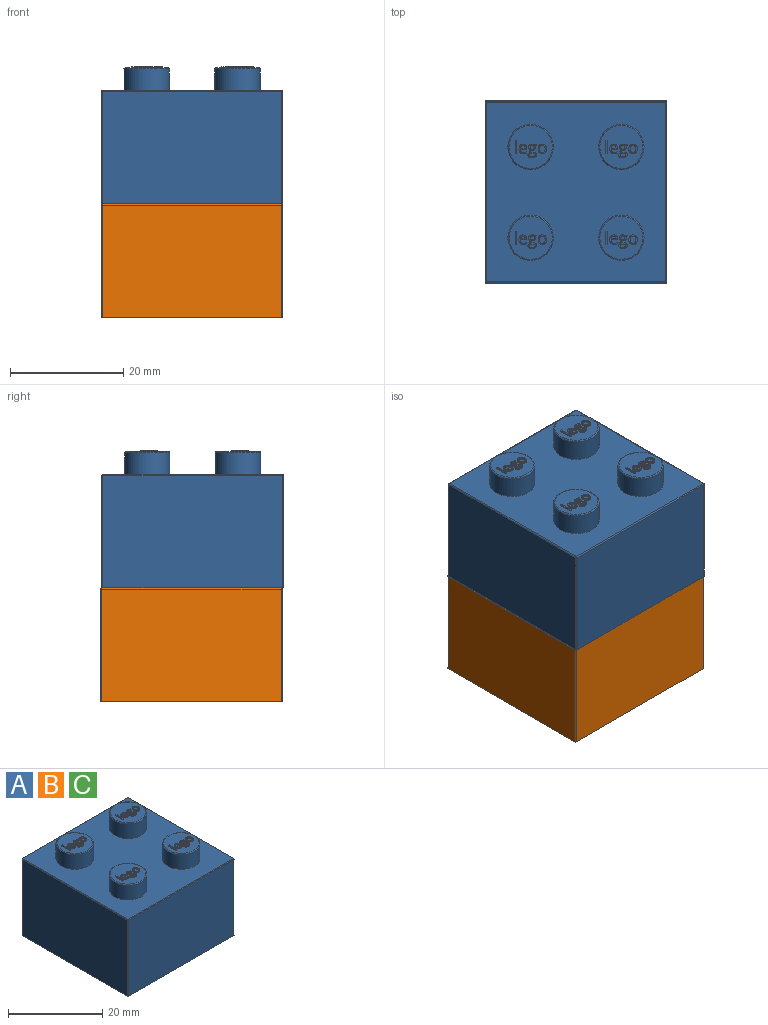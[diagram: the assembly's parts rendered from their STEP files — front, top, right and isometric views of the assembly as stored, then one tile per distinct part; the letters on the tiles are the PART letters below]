
ASSEMBLY  parts=3 mates=1
PART A: 411 faces, bbox 32x32x24.2 mm
  f0: plane 0.73x0.72mm, normal (0,0,1), area 0.4mm2, adj f12,f13,f14,f15,f16,f17
  f1: plane 1.04x0.58mm, normal (0,0,1), area 0.5mm2, adj f18,f19,f20,f21,f22,f23,f24,f25
  f2: plane 1.27x0.98mm, normal (0,0,1), area 1mm2, adj f57,f58,f59,f60,f61,f62,f63,f64
  f3: plane 0.85x0.48mm, normal (0,0,1), area 0.3mm2, adj f89,f90,f91,f92,f93
  f4: plane 0.73x0.72mm, normal (0,0,1), area 0.4mm2, adj f100,f101,f102,f103,f104,f105
  f5: plane 1.04x0.58mm, normal (0,0,1), area 0.5mm2, adj f106,f107,f108,f109,f110,f111,f112,f113
  f6: plane 1.27x0.98mm, normal (0,0,1), area 1mm2, adj f145,f146,f147,f148,f149,f150,f151,f152
  f7: plane 0.85x0.48mm, normal (0,0,1), area 0.3mm2, adj f177,f178,f179,f180,f181
  f8: plane 0.73x0.72mm, normal (0,0,1), area 0.4mm2, adj f188,f189,f190,f191,f192,f193
  f9: plane 1.04x0.58mm, normal (0,0,1), area 0.5mm2, adj f194,f195,f196,f197,f198,f199,f200,f201
  f10: plane 1.27x0.98mm, normal (0,0,1), area 1mm2, adj f233,f234,f235,f236,f237,f238,f239,f240
  f11: plane 0.85x0.48mm, normal (0,0,1), area 0.3mm2, adj f265,f266,f267,f268,f269
  f12: extruded ~0.27x0.2mm, area 0.1mm2, adj f0,f13,f17,f56
  f13: extruded ~0.36x0.35mm, area 0.1mm2, adj f0,f12,f14,f56
  f14: extruded ~0.37x0.36mm, area 0.1mm2, adj f0,f13,f15,f56
  f15: extruded ~0.27x0.2mm, area 0.1mm2, adj f0,f14,f16,f56
  f16: extruded ~0.28x0.2mm, area 0.1mm2, adj f0,f15,f17,f56
  f17: extruded ~0.26x0.2mm, area 0.1mm2, adj f0,f12,f16,f56
  f18: extruded ~0.32x0.2mm, area 0.1mm2, adj f1,f19,f26,f56
  f19: extruded ~0.46x0.2mm, area 0.1mm2, adj f1,f18,f20,f56
  f20: extruded ~0.25x0.2mm, area 0.1mm2, adj f1,f19,f21,f56
  f21: extruded ~0.2x0.18mm, area 0mm2, adj f1,f20,f22,f56
  f22: extruded ~0.31x0.2mm, area 0.1mm2, adj f1,f21,f23,f56
  f23: plane 0.3x0.2mm, normal (0,-1,0), area 0.1mm2, adj f1,f22,f24,f56
  f24: extruded ~0.26x0.2mm, area 0.1mm2, adj f1,f23,f25,f56
  f25: extruded ~0.23x0.2mm, area 0.1mm2, adj f1,f24,f26,f56
  f26: extruded ~0.2x0.2mm, area 0mm2, adj f1,f18,f25,f56
  f27: plane 0.3x0.2mm, normal (0.12,-0.99,0), area 0.1mm2, adj f28,f55,f56,f278
  f28: extruded ~0.2x0.14mm, area 0mm2, adj f27,f29,f56,f278
  f29: extruded ~0.2x0.19mm, area 0mm2, adj f28,f30,f56,f278
  f30: extruded ~0.38x0.2mm, area 0.1mm2, adj f29,f31,f56,f278
  f31: extruded ~0.45x0.2mm, area 0.1mm2, adj f30,f32,f56,f278
  f32: extruded ~0.2x0.14mm, area 0mm2, adj f31,f33,f56,f278
  f33: extruded ~0.21x0.2mm, area 0.1mm2, adj f32,f34,f56,f278
  f34: extruded ~0.2x0.1mm, area 0mm2, adj f33,f35,f56,f278
  f35: extruded ~0.2x0.19mm, area 0mm2, adj f34,f36,f56,f278
  f36: plane 0.29x0.2mm, normal (0,1,0), area 0.1mm2, adj f35,f37,f56,f278
  f37: extruded ~0.41x0.2mm, area 0.1mm2, adj f36,f38,f56,f278
  f38: extruded ~0.32x0.2mm, area 0.1mm2, adj f37,f39,f56,f278
  f39: extruded ~0.41x0.22mm, area 0.1mm2, adj f38,f40,f56,f278
  f40: extruded ~0.63x0.2mm, area 0.1mm2, adj f39,f41,f56,f278
  f41: extruded ~0.49x0.2mm, area 0.1mm2, adj f40,f42,f56,f278
  f42: extruded ~0.34x0.2mm, area 0.1mm2, adj f41,f43,f56,f278
  f43: extruded ~0.26x0.2mm, area 0.1mm2, adj f42,f44,f56,f278
  f44: extruded ~0.27x0.2mm, area 0.1mm2, adj f43,f45,f56,f278
  f45: extruded ~0.2x0.1mm, area 0mm2, adj f44,f46,f56,f278
  f46: extruded ~0.2x0.14mm, area 0mm2, adj f45,f47,f56,f278
  f47: extruded ~0.2x0.16mm, area 0mm2, adj f46,f48,f56,f278
  f48: extruded ~0.2x0.15mm, area 0mm2, adj f47,f49,f56,f278
  f49: extruded ~0.21x0.2mm, area 0.1mm2, adj f48,f50,f56,f278
  f50: extruded ~0.29x0.2mm, area 0.1mm2, adj f49,f51,f56,f278
  f51: extruded ~0.41x0.2mm, area 0.1mm2, adj f50,f52,f56,f278
  f52: extruded ~0.45x0.2mm, area 0.1mm2, adj f51,f53,f56,f278
  f53: extruded ~0.23x0.2mm, area 0mm2, adj f52,f54,f56,f278
  f54: plane 0.56x0.2mm, normal (0,1,0), area 0.1mm2, adj f53,f55,f56,f278
  f55: plane 0.2x0.16mm, normal (1,0,0), area 0mm2, adj f27,f54,f56,f278
  f56: plane 2.39x1.53mm, normal (0,0,1), area 1.5mm2, adj f12,f13,f14,f15,f16,f17,f18,f19
  f57: extruded ~0.37x0.2mm, area 0.1mm2, adj f2,f58,f64,f74
  f58: extruded ~0.37x0.2mm, area 0.1mm2, adj f2,f57,f59,f74
  f59: extruded ~0.48x0.2mm, area 0.1mm2, adj f2,f58,f60,f74
  f60: extruded ~0.47x0.2mm, area 0.1mm2, adj f2,f59,f61,f74
  f61: extruded ~0.37x0.2mm, area 0.1mm2, adj f2,f60,f62,f74
  f62: extruded ~0.37x0.2mm, area 0.1mm2, adj f2,f61,f63,f74
  f63: extruded ~0.47x0.2mm, area 0.1mm2, adj f2,f62,f64,f74
  f64: extruded ~0.48x0.2mm, area 0.1mm2, adj f2,f57,f63,f74
  f65: extruded ~0.55x0.22mm, area 0.1mm2, adj f66,f73,f74,f278
  f66: extruded ~0.39x0.2mm, area 0.1mm2, adj f65,f67,f74,f278
  f67: extruded ~0.29x0.26mm, area 0.1mm2, adj f66,f68,f74,f278
  f68: extruded ~0.45x0.2mm, area 0.1mm2, adj f67,f69,f74,f278
  f69: extruded ~0.62x0.2mm, area 0.1mm2, adj f68,f70,f74,f278
  f70: extruded ~0.55x0.22mm, area 0.1mm2, adj f69,f71,f74,f278
  f71: extruded ~0.54x0.23mm, area 0.1mm2, adj f70,f72,f74,f278
  f72: extruded ~0.61x0.2mm, area 0.1mm2, adj f71,f73,f74,f278
  f73: extruded ~0.62x0.2mm, area 0.1mm2, adj f65,f72,f74,f278
  f74: plane 1.69x1.49mm, normal (0,0,1), area 1mm2, adj f57,f58,f59,f60,f61,f62,f63,f64
  f75: extruded ~0.57x0.22mm, area 0.1mm2, adj f76,f88,f94,f278
  f76: extruded ~0.28x0.2mm, area 0.1mm2, adj f75,f77,f94,f278
  f77: extruded ~0.25x0.2mm, area 0.1mm2, adj f76,f78,f94,f278
  f78: plane 0.22x0.2mm, normal (1,0,0), area 0mm2, adj f77,f79,f94,f278
  f79: extruded ~0.52x0.2mm, area 0.1mm2, adj f78,f80,f94,f278
  f80: extruded ~0.39x0.2mm, area 0.1mm2, adj f79,f81,f94,f278
  f81: extruded ~0.43x0.2mm, area 0.1mm2, adj f80,f82,f94,f278
  f82: plane 1.12x0.2mm, normal (0,-1,0), area 0.2mm2, adj f81,f83,f94,f278
  f83: plane 0.2x0.16mm, normal (1,0,0), area 0mm2, adj f82,f84,f94,f278
  f84: extruded ~0.53x0.2mm, area 0.1mm2, adj f83,f85,f94,f278
  f85: extruded ~0.48x0.2mm, area 0.1mm2, adj f84,f86,f94,f278
  f86: extruded ~0.52x0.23mm, area 0.1mm2, adj f85,f87,f94,f278
  f87: extruded ~0.63x0.2mm, area 0.1mm2, adj f86,f88,f94,f278
  f88: extruded ~0.61x0.21mm, area 0.1mm2, adj f75,f87,f94,f278
  f89: extruded ~0.31x0.2mm, area 0.1mm2, adj f3,f90,f93,f94
  f90: extruded ~0.3x0.2mm, area 0.1mm2, adj f3,f89,f91,f94
  f91: extruded ~0.36x0.2mm, area 0.1mm2, adj f3,f90,f92,f94
  f92: plane 0.85x0.2mm, normal (0,1,0), area 0.2mm2, adj f3,f91,f93,f94
  f93: extruded ~0.35x0.2mm, area 0.1mm2, adj f3,f89,f92,f94
  f94: plane 1.69x1.38mm, normal (0,0,1), area 1.1mm2, adj f75,f76,f77,f78,f79,f80,f81,f82
  f95: plane 2.31x0.2mm, normal (-1,0,0), area 0.5mm2, adj f96,f98,f99,f278
  f96: plane 0.25x0.2mm, normal (0,1,0), area 0mm2, adj f95,f97,f99,f278
  f97: plane 2.31x0.2mm, normal (1,0,0), area 0.5mm2, adj f96,f98,f99,f278
  f98: plane 0.25x0.2mm, normal (0,-1,0), area 0mm2, adj f95,f97,f99,f278
  f99: plane 2.31x0.25mm, normal (0,0,1), area 0.6mm2, adj f95,f96,f97,f98
  f100: extruded ~0.27x0.2mm, area 0.1mm2, adj f4,f101,f105,f144
  f101: extruded ~0.36x0.35mm, area 0.1mm2, adj f4,f100,f102,f144
  f102: extruded ~0.37x0.36mm, area 0.1mm2, adj f4,f101,f103,f144
  f103: extruded ~0.27x0.2mm, area 0.1mm2, adj f4,f102,f104,f144
  f104: extruded ~0.28x0.2mm, area 0.1mm2, adj f4,f103,f105,f144
  f105: extruded ~0.26x0.2mm, area 0.1mm2, adj f4,f100,f104,f144
  f106: extruded ~0.32x0.2mm, area 0.1mm2, adj f5,f107,f114,f144
  f107: extruded ~0.46x0.2mm, area 0.1mm2, adj f5,f106,f108,f144
  f108: extruded ~0.25x0.2mm, area 0.1mm2, adj f5,f107,f109,f144
  f109: extruded ~0.2x0.18mm, area 0mm2, adj f5,f108,f110,f144
  f110: extruded ~0.31x0.2mm, area 0.1mm2, adj f5,f109,f111,f144
  f111: plane 0.3x0.2mm, normal (0,-1,0), area 0.1mm2, adj f5,f110,f112,f144
  f112: extruded ~0.26x0.2mm, area 0.1mm2, adj f5,f111,f113,f144
  f113: extruded ~0.23x0.2mm, area 0.1mm2, adj f5,f112,f114,f144
  f114: extruded ~0.2x0.2mm, area 0mm2, adj f5,f106,f113,f144
  f115: plane 0.3x0.2mm, normal (0.12,-0.99,0), area 0.1mm2, adj f116,f143,f144,f280
  f116: extruded ~0.2x0.14mm, area 0mm2, adj f115,f117,f144,f280
  f117: extruded ~0.2x0.19mm, area 0mm2, adj f116,f118,f144,f280
  f118: extruded ~0.38x0.2mm, area 0.1mm2, adj f117,f119,f144,f280
  f119: extruded ~0.45x0.2mm, area 0.1mm2, adj f118,f120,f144,f280
  f120: extruded ~0.2x0.14mm, area 0mm2, adj f119,f121,f144,f280
  f121: extruded ~0.21x0.2mm, area 0.1mm2, adj f120,f122,f144,f280
  f122: extruded ~0.2x0.1mm, area 0mm2, adj f121,f123,f144,f280
  f123: extruded ~0.2x0.19mm, area 0mm2, adj f122,f124,f144,f280
  f124: plane 0.29x0.2mm, normal (0,1,0), area 0.1mm2, adj f123,f125,f144,f280
  f125: extruded ~0.41x0.2mm, area 0.1mm2, adj f124,f126,f144,f280
  f126: extruded ~0.32x0.2mm, area 0.1mm2, adj f125,f127,f144,f280
  f127: extruded ~0.41x0.22mm, area 0.1mm2, adj f126,f128,f144,f280
  f128: extruded ~0.63x0.2mm, area 0.1mm2, adj f127,f129,f144,f280
  f129: extruded ~0.49x0.2mm, area 0.1mm2, adj f128,f130,f144,f280
  f130: extruded ~0.34x0.2mm, area 0.1mm2, adj f129,f131,f144,f280
  f131: extruded ~0.26x0.2mm, area 0.1mm2, adj f130,f132,f144,f280
  f132: extruded ~0.27x0.2mm, area 0.1mm2, adj f131,f133,f144,f280
  f133: extruded ~0.2x0.1mm, area 0mm2, adj f132,f134,f144,f280
  f134: extruded ~0.2x0.14mm, area 0mm2, adj f133,f135,f144,f280
  f135: extruded ~0.2x0.16mm, area 0mm2, adj f134,f136,f144,f280
  f136: extruded ~0.2x0.15mm, area 0mm2, adj f135,f137,f144,f280
  f137: extruded ~0.21x0.2mm, area 0.1mm2, adj f136,f138,f144,f280
  f138: extruded ~0.29x0.2mm, area 0.1mm2, adj f137,f139,f144,f280
  f139: extruded ~0.41x0.2mm, area 0.1mm2, adj f138,f140,f144,f280
  f140: extruded ~0.45x0.2mm, area 0.1mm2, adj f139,f141,f144,f280
  f141: extruded ~0.23x0.2mm, area 0mm2, adj f140,f142,f144,f280
  f142: plane 0.56x0.2mm, normal (0,1,0), area 0.1mm2, adj f141,f143,f144,f280
  f143: plane 0.2x0.16mm, normal (1,0,0), area 0mm2, adj f115,f142,f144,f280
  f144: plane 2.39x1.53mm, normal (0,0,1), area 1.5mm2, adj f100,f101,f102,f103,f104,f105,f106,f107
  f145: extruded ~0.37x0.2mm, area 0.1mm2, adj f6,f146,f152,f162
  f146: extruded ~0.37x0.2mm, area 0.1mm2, adj f6,f145,f147,f162
  f147: extruded ~0.48x0.2mm, area 0.1mm2, adj f6,f146,f148,f162
  f148: extruded ~0.47x0.2mm, area 0.1mm2, adj f6,f147,f149,f162
  f149: extruded ~0.37x0.2mm, area 0.1mm2, adj f6,f148,f150,f162
  f150: extruded ~0.37x0.2mm, area 0.1mm2, adj f6,f149,f151,f162
  f151: extruded ~0.47x0.2mm, area 0.1mm2, adj f6,f150,f152,f162
  f152: extruded ~0.48x0.2mm, area 0.1mm2, adj f6,f145,f151,f162
  f153: extruded ~0.55x0.22mm, area 0.1mm2, adj f154,f161,f162,f280
  f154: extruded ~0.39x0.2mm, area 0.1mm2, adj f153,f155,f162,f280
  f155: extruded ~0.29x0.26mm, area 0.1mm2, adj f154,f156,f162,f280
  f156: extruded ~0.45x0.2mm, area 0.1mm2, adj f155,f157,f162,f280
  f157: extruded ~0.62x0.2mm, area 0.1mm2, adj f156,f158,f162,f280
  f158: extruded ~0.55x0.22mm, area 0.1mm2, adj f157,f159,f162,f280
  f159: extruded ~0.54x0.23mm, area 0.1mm2, adj f158,f160,f162,f280
  f160: extruded ~0.61x0.2mm, area 0.1mm2, adj f159,f161,f162,f280
  f161: extruded ~0.62x0.2mm, area 0.1mm2, adj f153,f160,f162,f280
  f162: plane 1.69x1.49mm, normal (0,0,1), area 1mm2, adj f145,f146,f147,f148,f149,f150,f151,f152
  f163: extruded ~0.57x0.22mm, area 0.1mm2, adj f164,f176,f182,f280
  f164: extruded ~0.28x0.2mm, area 0.1mm2, adj f163,f165,f182,f280
  f165: extruded ~0.25x0.2mm, area 0.1mm2, adj f164,f166,f182,f280
  f166: plane 0.22x0.2mm, normal (1,0,0), area 0mm2, adj f165,f167,f182,f280
  f167: extruded ~0.52x0.2mm, area 0.1mm2, adj f166,f168,f182,f280
  f168: extruded ~0.39x0.2mm, area 0.1mm2, adj f167,f169,f182,f280
  f169: extruded ~0.43x0.2mm, area 0.1mm2, adj f168,f170,f182,f280
  f170: plane 1.12x0.2mm, normal (0,-1,0), area 0.2mm2, adj f169,f171,f182,f280
  f171: plane 0.2x0.16mm, normal (1,0,0), area 0mm2, adj f170,f172,f182,f280
  f172: extruded ~0.53x0.2mm, area 0.1mm2, adj f171,f173,f182,f280
  f173: extruded ~0.48x0.2mm, area 0.1mm2, adj f172,f174,f182,f280
  f174: extruded ~0.52x0.23mm, area 0.1mm2, adj f173,f175,f182,f280
  f175: extruded ~0.63x0.2mm, area 0.1mm2, adj f174,f176,f182,f280
  f176: extruded ~0.61x0.21mm, area 0.1mm2, adj f163,f175,f182,f280
  f177: extruded ~0.31x0.2mm, area 0.1mm2, adj f7,f178,f181,f182
  f178: extruded ~0.3x0.2mm, area 0.1mm2, adj f7,f177,f179,f182
  f179: extruded ~0.36x0.2mm, area 0.1mm2, adj f7,f178,f180,f182
  f180: plane 0.85x0.2mm, normal (0,1,0), area 0.2mm2, adj f7,f179,f181,f182
  f181: extruded ~0.35x0.2mm, area 0.1mm2, adj f7,f177,f180,f182
  f182: plane 1.69x1.38mm, normal (0,0,1), area 1.1mm2, adj f163,f164,f165,f166,f167,f168,f169,f170
  f183: plane 2.31x0.2mm, normal (-1,0,0), area 0.5mm2, adj f184,f186,f187,f280
  f184: plane 0.25x0.2mm, normal (0,1,0), area 0mm2, adj f183,f185,f187,f280
  f185: plane 2.31x0.2mm, normal (1,0,0), area 0.5mm2, adj f184,f186,f187,f280
  f186: plane 0.25x0.2mm, normal (0,-1,0), area 0mm2, adj f183,f185,f187,f280
  f187: plane 2.31x0.25mm, normal (0,0,1), area 0.6mm2, adj f183,f184,f185,f186
  f188: extruded ~0.27x0.2mm, area 0.1mm2, adj f8,f189,f193,f232
  f189: extruded ~0.36x0.35mm, area 0.1mm2, adj f8,f188,f190,f232
  f190: extruded ~0.37x0.36mm, area 0.1mm2, adj f8,f189,f191,f232
  f191: extruded ~0.27x0.2mm, area 0.1mm2, adj f8,f190,f192,f232
  f192: extruded ~0.28x0.2mm, area 0.1mm2, adj f8,f191,f193,f232
  f193: extruded ~0.26x0.2mm, area 0.1mm2, adj f8,f188,f192,f232
  f194: extruded ~0.32x0.2mm, area 0.1mm2, adj f9,f195,f202,f232
  f195: extruded ~0.46x0.2mm, area 0.1mm2, adj f9,f194,f196,f232
  f196: extruded ~0.25x0.2mm, area 0.1mm2, adj f9,f195,f197,f232
  f197: extruded ~0.2x0.18mm, area 0mm2, adj f9,f196,f198,f232
  f198: extruded ~0.31x0.2mm, area 0.1mm2, adj f9,f197,f199,f232
  f199: plane 0.3x0.2mm, normal (0,-1,0), area 0.1mm2, adj f9,f198,f200,f232
  f200: extruded ~0.26x0.2mm, area 0.1mm2, adj f9,f199,f201,f232
  f201: extruded ~0.23x0.2mm, area 0.1mm2, adj f9,f200,f202,f232
  f202: extruded ~0.2x0.2mm, area 0mm2, adj f9,f194,f201,f232
  f203: plane 0.3x0.2mm, normal (0.12,-0.99,0), area 0.1mm2, adj f204,f231,f232,f282
  f204: extruded ~0.2x0.14mm, area 0mm2, adj f203,f205,f232,f282
  f205: extruded ~0.2x0.19mm, area 0mm2, adj f204,f206,f232,f282
  f206: extruded ~0.38x0.2mm, area 0.1mm2, adj f205,f207,f232,f282
  f207: extruded ~0.45x0.2mm, area 0.1mm2, adj f206,f208,f232,f282
  f208: extruded ~0.2x0.14mm, area 0mm2, adj f207,f209,f232,f282
  f209: extruded ~0.21x0.2mm, area 0.1mm2, adj f208,f210,f232,f282
  f210: extruded ~0.2x0.1mm, area 0mm2, adj f209,f211,f232,f282
  f211: extruded ~0.2x0.19mm, area 0mm2, adj f210,f212,f232,f282
  f212: plane 0.29x0.2mm, normal (0,1,0), area 0.1mm2, adj f211,f213,f232,f282
  f213: extruded ~0.41x0.2mm, area 0.1mm2, adj f212,f214,f232,f282
  f214: extruded ~0.32x0.2mm, area 0.1mm2, adj f213,f215,f232,f282
  f215: extruded ~0.41x0.22mm, area 0.1mm2, adj f214,f216,f232,f282
  f216: extruded ~0.63x0.2mm, area 0.1mm2, adj f215,f217,f232,f282
  f217: extruded ~0.49x0.2mm, area 0.1mm2, adj f216,f218,f232,f282
  f218: extruded ~0.34x0.2mm, area 0.1mm2, adj f217,f219,f232,f282
  f219: extruded ~0.26x0.2mm, area 0.1mm2, adj f218,f220,f232,f282
  f220: extruded ~0.27x0.2mm, area 0.1mm2, adj f219,f221,f232,f282
  f221: extruded ~0.2x0.1mm, area 0mm2, adj f220,f222,f232,f282
  f222: extruded ~0.2x0.14mm, area 0mm2, adj f221,f223,f232,f282
  f223: extruded ~0.2x0.16mm, area 0mm2, adj f222,f224,f232,f282
  f224: extruded ~0.2x0.15mm, area 0mm2, adj f223,f225,f232,f282
  f225: extruded ~0.21x0.2mm, area 0.1mm2, adj f224,f226,f232,f282
  f226: extruded ~0.29x0.2mm, area 0.1mm2, adj f225,f227,f232,f282
  f227: extruded ~0.41x0.2mm, area 0.1mm2, adj f226,f228,f232,f282
  f228: extruded ~0.45x0.2mm, area 0.1mm2, adj f227,f229,f232,f282
  f229: extruded ~0.23x0.2mm, area 0mm2, adj f228,f230,f232,f282
  f230: plane 0.56x0.2mm, normal (0,1,0), area 0.1mm2, adj f229,f231,f232,f282
  f231: plane 0.2x0.16mm, normal (1,0,0), area 0mm2, adj f203,f230,f232,f282
  f232: plane 2.39x1.53mm, normal (0,0,1), area 1.5mm2, adj f188,f189,f190,f191,f192,f193,f194,f195
  f233: extruded ~0.37x0.2mm, area 0.1mm2, adj f10,f234,f240,f250
  f234: extruded ~0.37x0.2mm, area 0.1mm2, adj f10,f233,f235,f250
  f235: extruded ~0.48x0.2mm, area 0.1mm2, adj f10,f234,f236,f250
  f236: extruded ~0.47x0.2mm, area 0.1mm2, adj f10,f235,f237,f250
  f237: extruded ~0.37x0.2mm, area 0.1mm2, adj f10,f236,f238,f250
  f238: extruded ~0.37x0.2mm, area 0.1mm2, adj f10,f237,f239,f250
  f239: extruded ~0.47x0.2mm, area 0.1mm2, adj f10,f238,f240,f250
  f240: extruded ~0.48x0.2mm, area 0.1mm2, adj f10,f233,f239,f250
  f241: extruded ~0.55x0.22mm, area 0.1mm2, adj f242,f249,f250,f282
  f242: extruded ~0.39x0.2mm, area 0.1mm2, adj f241,f243,f250,f282
  f243: extruded ~0.29x0.26mm, area 0.1mm2, adj f242,f244,f250,f282
  f244: extruded ~0.45x0.2mm, area 0.1mm2, adj f243,f245,f250,f282
  f245: extruded ~0.62x0.2mm, area 0.1mm2, adj f244,f246,f250,f282
  f246: extruded ~0.55x0.22mm, area 0.1mm2, adj f245,f247,f250,f282
  f247: extruded ~0.54x0.23mm, area 0.1mm2, adj f246,f248,f250,f282
  f248: extruded ~0.61x0.2mm, area 0.1mm2, adj f247,f249,f250,f282
  f249: extruded ~0.62x0.2mm, area 0.1mm2, adj f241,f248,f250,f282
  f250: plane 1.69x1.49mm, normal (0,0,1), area 1mm2, adj f233,f234,f235,f236,f237,f238,f239,f240
  f251: extruded ~0.57x0.22mm, area 0.1mm2, adj f252,f264,f270,f282
  f252: extruded ~0.28x0.2mm, area 0.1mm2, adj f251,f253,f270,f282
  f253: extruded ~0.25x0.2mm, area 0.1mm2, adj f252,f254,f270,f282
  f254: plane 0.22x0.2mm, normal (1,0,0), area 0mm2, adj f253,f255,f270,f282
  f255: extruded ~0.52x0.2mm, area 0.1mm2, adj f254,f256,f270,f282
  f256: extruded ~0.39x0.2mm, area 0.1mm2, adj f255,f257,f270,f282
  f257: extruded ~0.43x0.2mm, area 0.1mm2, adj f256,f258,f270,f282
  f258: plane 1.12x0.2mm, normal (0,-1,0), area 0.2mm2, adj f257,f259,f270,f282
  f259: plane 0.2x0.16mm, normal (1,0,0), area 0mm2, adj f258,f260,f270,f282
  f260: extruded ~0.53x0.2mm, area 0.1mm2, adj f259,f261,f270,f282
  f261: extruded ~0.48x0.2mm, area 0.1mm2, adj f260,f262,f270,f282
  f262: extruded ~0.52x0.23mm, area 0.1mm2, adj f261,f263,f270,f282
  f263: extruded ~0.63x0.2mm, area 0.1mm2, adj f262,f264,f270,f282
  f264: extruded ~0.61x0.21mm, area 0.1mm2, adj f251,f263,f270,f282
  f265: extruded ~0.31x0.2mm, area 0.1mm2, adj f11,f266,f269,f270
  f266: extruded ~0.3x0.2mm, area 0.1mm2, adj f11,f265,f267,f270
  f267: extruded ~0.36x0.2mm, area 0.1mm2, adj f11,f266,f268,f270
  f268: plane 0.85x0.2mm, normal (0,1,0), area 0.2mm2, adj f11,f267,f269,f270
  f269: extruded ~0.35x0.2mm, area 0.1mm2, adj f11,f265,f268,f270
  f270: plane 1.69x1.38mm, normal (0,0,1), area 1.1mm2, adj f251,f252,f253,f254,f255,f256,f257,f258
  f271: plane 2.31x0.2mm, normal (-1,0,0), area 0.5mm2, adj f272,f274,f275,f282
  f272: plane 0.25x0.2mm, normal (0,1,0), area 0mm2, adj f271,f273,f275,f282
  f273: plane 2.31x0.2mm, normal (1,0,0), area 0.5mm2, adj f272,f274,f275,f282
  f274: plane 0.25x0.2mm, normal (0,-1,0), area 0mm2, adj f271,f273,f275,f282
  f275: plane 2.31x0.25mm, normal (0,0,1), area 0.6mm2, adj f271,f272,f273,f274
  f276: plane 7.6x7.6mm, normal (0,0,1), area 38.9mm2, adj f293,f319,f320,f321,f322,f328,f329,f330
  f277: cylinder r=4mm len=8mm, axis (0,0,-1), area 95.5mm2, adj f287,f290
  f278: plane 7.6x7.6mm, normal (0,0,1), area 38.9mm2, adj f27,f28,f29,f30,f31,f32,f33,f34
  f279: cylinder r=4mm len=8mm, axis (0,0,-1), area 95.5mm2, adj f287,f291
  f280: plane 7.6x7.6mm, normal (0,0,1), area 38.9mm2, adj f115,f116,f117,f118,f119,f120,f121,f122
  f281: cylinder r=4mm len=8mm, axis (0,0,-1), area 95.5mm2, adj f287,f292
  f282: plane 7.6x7.6mm, normal (0,0,1), area 38.9mm2, adj f203,f204,f205,f206,f207,f208,f209,f210
  f283: plane 31.6x19.8mm, normal (1,0,0), area 625.7mm2, adj f288,f296,f302,f305
  f284: plane 31.6x19.8mm, normal (0,1,0), area 625.7mm2, adj f288,f299,f303,f305
  f285: plane 31.6x19.8mm, normal (-1,0,0), area 625.7mm2, adj f288,f294,f298,f299
  f286: plane 31.6x19.8mm, normal (0,-1,0), area 625.7mm2, adj f288,f294,f296,f297
  f287: plane 31.6x31.6mm, normal (0,0,1), area 797.5mm2, adj f277,f279,f281,f289,f297,f298,f302,f303
  f288: plane 32x32mm, normal (0,0,-1), area 240mm2, adj f283,f284,f285,f286,f294,f296,f299,f305
  f289: cylinder r=4mm len=8mm, axis (0,0,-1), area 95.5mm2, adj f287,f293
  f290: torus R=3.8mm, axis (0,0,1), area 7.8mm2, adj f277,f278
  f291: torus R=3.8mm, axis (0,0,1), area 7.8mm2, adj f279,f280
  f292: torus R=3.8mm, axis (0,0,1), area 7.8mm2, adj f281,f282
  f293: torus R=3.8mm, axis (0,0,1), area 7.8mm2, adj f276,f289
  f294: cylinder r=0.2mm len=19.8mm, axis (0,0,1), area 6.2mm2, adj f285,f286,f288,f295
  f295: sphere r=0.2mm, area 0.1mm2, adj f294,f297,f298
  f296: cylinder r=0.2mm len=19.8mm, axis (0,0,-1), area 6.2mm2, adj f283,f286,f288,f300
  f297: cylinder r=0.2mm len=31.6mm, axis (-1,0,0), area 9.9mm2, adj f286,f287,f295,f300
  f298: cylinder r=0.2mm len=31.6mm, axis (0,1,0), area 9.9mm2, adj f285,f287,f295,f301
  f299: cylinder r=0.2mm len=19.8mm, axis (0,0,-1), area 6.2mm2, adj f284,f285,f288,f301
  f300: sphere r=0.2mm, area 0.1mm2, adj f296,f297,f302
  f301: sphere r=0.2mm, area 0.1mm2, adj f298,f299,f303
  f302: cylinder r=0.2mm len=31.6mm, axis (0,-1,0), area 9.9mm2, adj f283,f287,f300,f304
  f303: cylinder r=0.2mm len=31.6mm, axis (1,0,0), area 9.9mm2, adj f284,f287,f301,f304
  f304: sphere r=0.2mm, area 0.1mm2, adj f302,f303,f305
  f305: cylinder r=0.2mm len=19.8mm, axis (0,0,1), area 6.2mm2, adj f283,f284,f288,f304
  f306: cylinder r=2mm len=4mm, axis (0,0,-1), area 50.3mm2, adj f307,f316
  f307: plane 4x4mm, normal (0,0,-1), area 12.6mm2, adj f306
  f308: cylinder r=2mm len=4mm, axis (0,0,-1), area 50.3mm2, adj f309,f316
  f309: plane 4x4mm, normal (0,0,-1), area 12.6mm2, adj f308
  f310: cylinder r=2mm len=4mm, axis (0,0,-1), area 50.3mm2, adj f311,f316
  f311: plane 4x4mm, normal (0,0,-1), area 12.6mm2, adj f310
  f312: plane 28x18mm, normal (-1,0,0), area 504mm2, adj f288,f313,f315,f316
  f313: plane 28x18mm, normal (0,-1,0), area 504mm2, adj f288,f312,f314,f316
  f314: plane 28x18mm, normal (1,0,0), area 504mm2, adj f288,f313,f315,f316
  f315: plane 28x18mm, normal (0,1,0), area 504mm2, adj f288,f312,f314,f316
  f316: plane 28x28mm, normal (0,0,-1), area 733.7mm2, adj f306,f308,f310,f312,f313,f314,f315,f317
  f317: cylinder r=2mm len=4mm, axis (0,0,-1), area 50.3mm2, adj f316,f318
  f318: plane 4x4mm, normal (0,0,-1), area 12.6mm2, adj f317
  f319: plane 0.25x0.2mm, normal (0,-1,0), area 0mm2, adj f276,f320,f322,f323
  f320: plane 2.31x0.2mm, normal (1,0,0), area 0.5mm2, adj f276,f319,f321,f323
  f321: plane 0.25x0.2mm, normal (0,1,0), area 0mm2, adj f276,f320,f322,f323
  f322: plane 2.31x0.2mm, normal (-1,0,0), area 0.5mm2, adj f276,f319,f321,f323
  f323: plane 2.31x0.25mm, normal (0,0,1), area 0.6mm2, adj f319,f320,f321,f322
  f324: extruded ~0.31x0.2mm, area 0.1mm2, adj f325,f342,f343,f344
  f325: extruded ~0.3x0.2mm, area 0.1mm2, adj f324,f326,f343,f344
  f326: extruded ~0.36x0.2mm, area 0.1mm2, adj f325,f327,f343,f344
  f327: plane 0.85x0.2mm, normal (0,1,0), area 0.2mm2, adj f326,f342,f343,f344
  f328: extruded ~0.57x0.22mm, area 0.1mm2, adj f276,f329,f341,f343
  f329: extruded ~0.28x0.2mm, area 0.1mm2, adj f276,f328,f330,f343
  f330: extruded ~0.25x0.2mm, area 0.1mm2, adj f276,f329,f331,f343
  f331: plane 0.22x0.2mm, normal (1,0,0), area 0mm2, adj f276,f330,f332,f343
  f332: extruded ~0.52x0.2mm, area 0.1mm2, adj f276,f331,f333,f343
  f333: extruded ~0.39x0.2mm, area 0.1mm2, adj f276,f332,f334,f343
  f334: extruded ~0.43x0.2mm, area 0.1mm2, adj f276,f333,f335,f343
  f335: plane 1.12x0.2mm, normal (0,-1,0), area 0.2mm2, adj f276,f334,f336,f343
  f336: plane 0.2x0.16mm, normal (1,0,0), area 0mm2, adj f276,f335,f337,f343
  f337: extruded ~0.53x0.2mm, area 0.1mm2, adj f276,f336,f338,f343
  f338: extruded ~0.48x0.2mm, area 0.1mm2, adj f276,f337,f339,f343
  f339: extruded ~0.52x0.23mm, area 0.1mm2, adj f276,f338,f340,f343
  f340: extruded ~0.63x0.2mm, area 0.1mm2, adj f276,f339,f341,f343
  f341: extruded ~0.61x0.21mm, area 0.1mm2, adj f276,f328,f340,f343
  f342: extruded ~0.35x0.2mm, area 0.1mm2, adj f324,f327,f343,f344
  f343: plane 1.69x1.38mm, normal (0,0,1), area 1.1mm2, adj f324,f325,f326,f327,f328,f329,f330,f331
  f344: plane 0.85x0.48mm, normal (0,0,1), area 0.3mm2, adj f324,f325,f326,f327,f342
  f345: extruded ~0.26x0.2mm, area 0.1mm2, adj f346,f388,f389,f390
  f346: extruded ~0.28x0.2mm, area 0.1mm2, adj f345,f347,f389,f390
  f347: extruded ~0.27x0.2mm, area 0.1mm2, adj f346,f348,f389,f390
  f348: extruded ~0.37x0.36mm, area 0.1mm2, adj f347,f349,f389,f390
  f349: extruded ~0.36x0.35mm, area 0.1mm2, adj f348,f388,f389,f390
  f350: extruded ~0.2x0.2mm, area 0mm2, adj f351,f386,f389,f391
  f351: extruded ~0.23x0.2mm, area 0.1mm2, adj f350,f352,f389,f391
  f352: extruded ~0.26x0.2mm, area 0.1mm2, adj f351,f353,f389,f391
  f353: plane 0.3x0.2mm, normal (0,-1,0), area 0.1mm2, adj f352,f354,f389,f391
  f354: extruded ~0.31x0.2mm, area 0.1mm2, adj f353,f355,f389,f391
  f355: extruded ~0.2x0.18mm, area 0mm2, adj f354,f356,f389,f391
  f356: extruded ~0.25x0.2mm, area 0.1mm2, adj f355,f357,f389,f391
  f357: extruded ~0.46x0.2mm, area 0.1mm2, adj f356,f386,f389,f391
  f358: plane 0.2x0.16mm, normal (1,0,0), area 0mm2, adj f276,f359,f387,f389
  f359: plane 0.56x0.2mm, normal (0,1,0), area 0.1mm2, adj f276,f358,f360,f389
  f360: extruded ~0.23x0.2mm, area 0mm2, adj f276,f359,f361,f389
  f361: extruded ~0.45x0.2mm, area 0.1mm2, adj f276,f360,f362,f389
  f362: extruded ~0.41x0.2mm, area 0.1mm2, adj f276,f361,f363,f389
  f363: extruded ~0.29x0.2mm, area 0.1mm2, adj f276,f362,f364,f389
  f364: extruded ~0.21x0.2mm, area 0.1mm2, adj f276,f363,f365,f389
  f365: extruded ~0.2x0.15mm, area 0mm2, adj f276,f364,f366,f389
  f366: extruded ~0.2x0.16mm, area 0mm2, adj f276,f365,f367,f389
  f367: extruded ~0.2x0.14mm, area 0mm2, adj f276,f366,f368,f389
  f368: extruded ~0.2x0.1mm, area 0mm2, adj f276,f367,f369,f389
  f369: extruded ~0.27x0.2mm, area 0.1mm2, adj f276,f368,f370,f389
  f370: extruded ~0.26x0.2mm, area 0.1mm2, adj f276,f369,f371,f389
  f371: extruded ~0.34x0.2mm, area 0.1mm2, adj f276,f370,f372,f389
  f372: extruded ~0.49x0.2mm, area 0.1mm2, adj f276,f371,f373,f389
  f373: extruded ~0.63x0.2mm, area 0.1mm2, adj f276,f372,f374,f389
  f374: extruded ~0.41x0.22mm, area 0.1mm2, adj f276,f373,f375,f389
  f375: extruded ~0.32x0.2mm, area 0.1mm2, adj f276,f374,f376,f389
  f376: extruded ~0.41x0.2mm, area 0.1mm2, adj f276,f375,f377,f389
  f377: plane 0.29x0.2mm, normal (0,1,0), area 0.1mm2, adj f276,f376,f378,f389
  f378: extruded ~0.2x0.19mm, area 0mm2, adj f276,f377,f379,f389
  f379: extruded ~0.2x0.1mm, area 0mm2, adj f276,f378,f380,f389
  f380: extruded ~0.21x0.2mm, area 0.1mm2, adj f276,f379,f381,f389
  f381: extruded ~0.2x0.14mm, area 0mm2, adj f276,f380,f382,f389
  f382: extruded ~0.45x0.2mm, area 0.1mm2, adj f276,f381,f383,f389
  f383: extruded ~0.38x0.2mm, area 0.1mm2, adj f276,f382,f384,f389
  f384: extruded ~0.2x0.19mm, area 0mm2, adj f276,f383,f385,f389
  f385: extruded ~0.2x0.14mm, area 0mm2, adj f276,f384,f387,f389
  f386: extruded ~0.32x0.2mm, area 0.1mm2, adj f350,f357,f389,f391
  f387: plane 0.3x0.2mm, normal (0.12,-0.99,0), area 0.1mm2, adj f276,f358,f385,f389
  f388: extruded ~0.27x0.2mm, area 0.1mm2, adj f345,f349,f389,f390
  f389: plane 2.39x1.53mm, normal (0,0,1), area 1.5mm2, adj f345,f346,f347,f348,f349,f350,f351,f352
  f390: plane 0.73x0.72mm, normal (0,0,1), area 0.4mm2, adj f345,f346,f347,f348,f349,f388
  f391: plane 1.04x0.58mm, normal (0,0,1), area 0.5mm2, adj f350,f351,f352,f353,f354,f355,f356,f357
  f392: extruded ~0.48x0.2mm, area 0.1mm2, adj f393,f408,f409,f410
  f393: extruded ~0.47x0.2mm, area 0.1mm2, adj f392,f394,f409,f410
  f394: extruded ~0.37x0.2mm, area 0.1mm2, adj f393,f395,f409,f410
  f395: extruded ~0.37x0.2mm, area 0.1mm2, adj f394,f396,f409,f410
  f396: extruded ~0.47x0.2mm, area 0.1mm2, adj f395,f397,f409,f410
  f397: extruded ~0.48x0.2mm, area 0.1mm2, adj f396,f398,f409,f410
  f398: extruded ~0.37x0.2mm, area 0.1mm2, adj f397,f408,f409,f410
  f399: extruded ~0.62x0.2mm, area 0.1mm2, adj f276,f400,f407,f409
  f400: extruded ~0.61x0.2mm, area 0.1mm2, adj f276,f399,f401,f409
  f401: extruded ~0.54x0.23mm, area 0.1mm2, adj f276,f400,f402,f409
  f402: extruded ~0.55x0.22mm, area 0.1mm2, adj f276,f401,f403,f409
  f403: extruded ~0.62x0.2mm, area 0.1mm2, adj f276,f402,f404,f409
  f404: extruded ~0.45x0.2mm, area 0.1mm2, adj f276,f403,f405,f409
  f405: extruded ~0.29x0.26mm, area 0.1mm2, adj f276,f404,f406,f409
  f406: extruded ~0.39x0.2mm, area 0.1mm2, adj f276,f405,f407,f409
  f407: extruded ~0.55x0.22mm, area 0.1mm2, adj f276,f399,f406,f409
  f408: extruded ~0.37x0.2mm, area 0.1mm2, adj f392,f398,f409,f410
  f409: plane 1.69x1.49mm, normal (0,0,1), area 1mm2, adj f392,f393,f394,f395,f396,f397,f398,f399
  f410: plane 1.27x0.98mm, normal (0,0,1), area 1mm2, adj f392,f393,f394,f395,f396,f397,f398,f408
PART B: same geometry as A
PART C: same geometry as A
PLACE A t=(-10.71,0.4,18.08)mm
PLACE B t=(-10.71,0.6,-1.92)mm
PLACE C t=(-10.71,0.6,-1.92)mm fixed
MATE parallel C.f305 <-> A.f288  axis (0,0,1) through (5.09,16.4,18.08)mm
